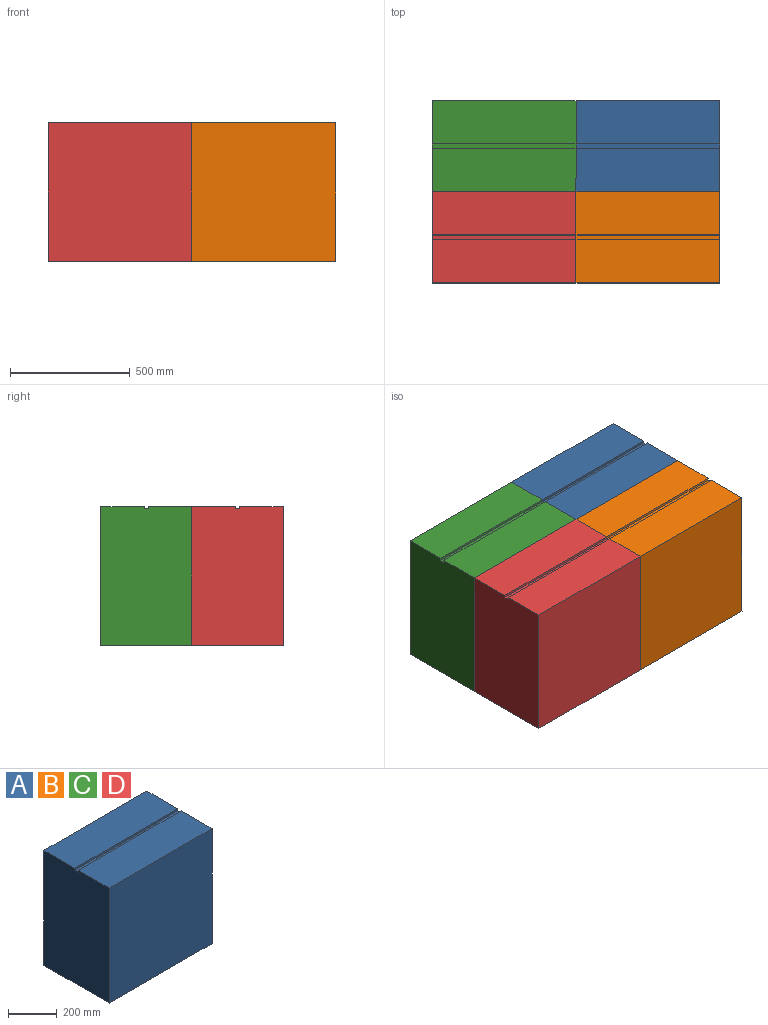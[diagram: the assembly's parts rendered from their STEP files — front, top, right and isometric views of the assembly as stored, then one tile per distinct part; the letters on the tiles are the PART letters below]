
ASSEMBLY  parts=4 mates=3
PART A: 10 faces, bbox 600x380x580 mm
  f0: plane 600x180mm, normal (0,0,1), area 108000mm2, adj f1,f2,f3,f8
  f1: plane 580x380mm, normal (-1,0,0), area 220200mm2, adj f0,f3,f4,f5,f6,f7,f8,f9
  f2: plane 580x380mm, normal (1,0,0), area 220200mm2, adj f0,f3,f4,f5,f6,f7,f8,f9
  f3: plane 600x580mm, normal (0,-1,0), area 348000mm2, adj f0,f1,f2,f4
  f4: plane 600x380mm, normal (0,0,-1), area 228000mm2, adj f1,f2,f3,f5
  f5: plane 600x580mm, normal (0,1,0), area 348000mm2, adj f1,f2,f4,f6
  f6: plane 600x180mm, normal (0,0,1), area 108000mm2, adj f1,f2,f5,f7
  f7: plane 600x10mm, normal (0,-1,0), area 6000mm2, adj f1,f2,f6,f9
  f8: plane 600x10mm, normal (0,1,0), area 6000mm2, adj f0,f1,f2,f9
  f9: plane 600x20mm, normal (0,0,1), area 12000mm2, adj f1,f2,f7,f8
PART B: same geometry as A
PART C: same geometry as A
PART D: same geometry as A
PLACE A t=(732.14,191.77,419.71)mm
PLACE B t=(732.14,-188.23,419.71)mm
PLACE C t=(132.14,191.77,419.71)mm
PLACE D t=(132.14,-188.23,419.71)mm
MATE fastened C.f2 <-> A.f1  axis (1,0,0) through (132.14,31.16,863.27)mm
MATE fastened A.f3 <-> B.f5  axis (0,-1,0) through (732.14,31.16,863.27)mm
MATE fastened B.f1 <-> D.f2  axis (-1,0,0) through (132.14,-348.84,863.27)mm
